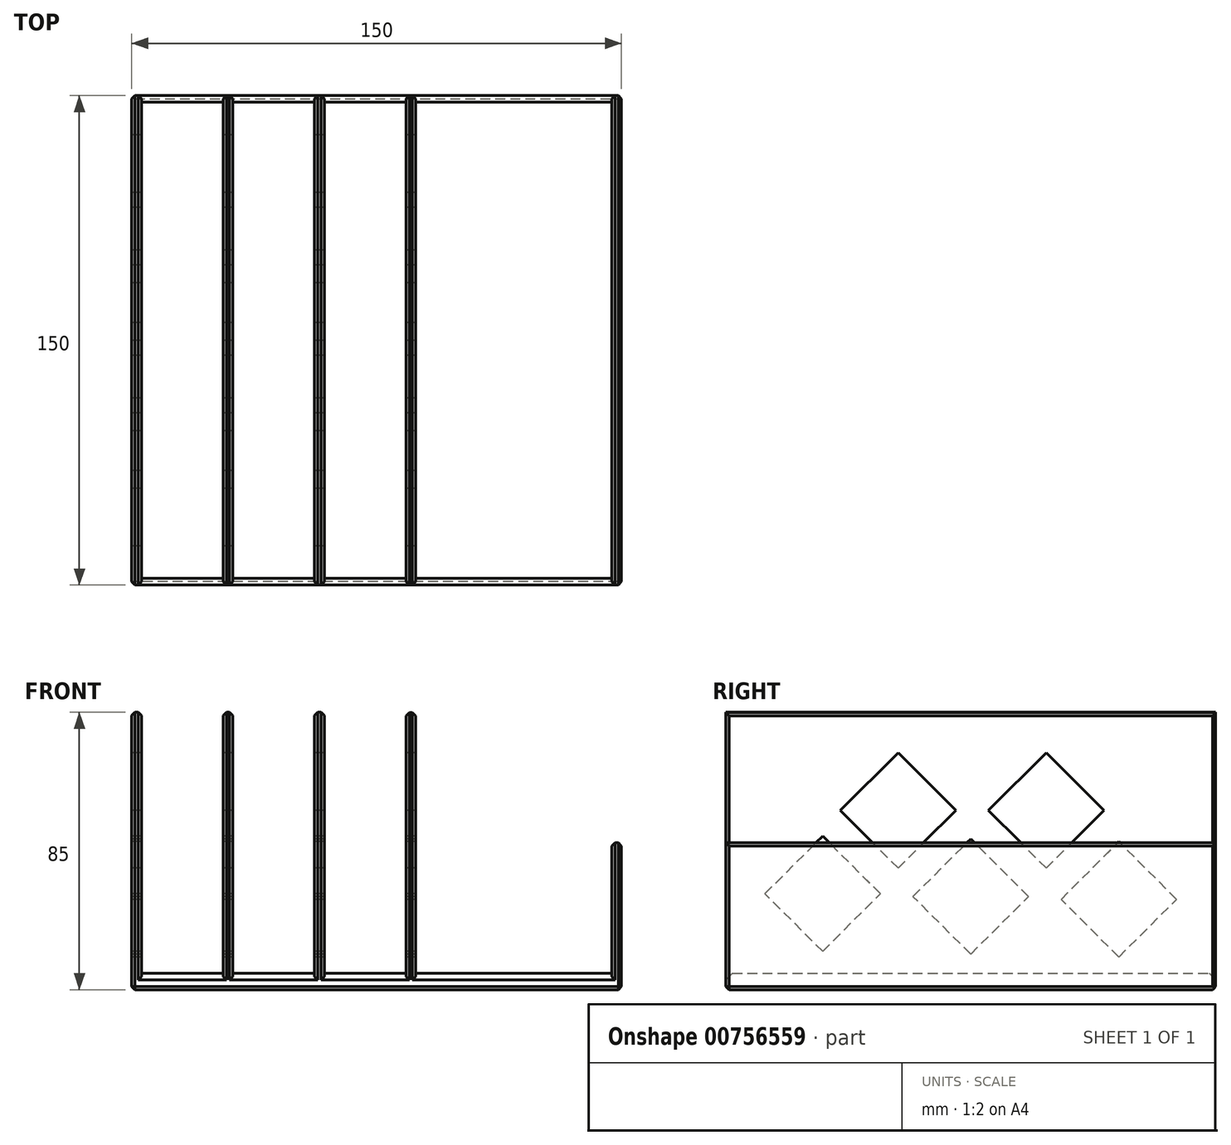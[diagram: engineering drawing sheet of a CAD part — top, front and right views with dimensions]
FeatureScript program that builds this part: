
annotation { "Feature Type Name" : "Feature", "Feature Type Description" : "" }
export const myFeature = defineFeature(function(context is Context, id is Id, definition is map)
    precondition{}
    {
        {
            var Q0;
            Q0=qCreatedBy(makeId("Front.planeOp"),FACE);
            var sketch = newSketch(context, id + "F0", { "sketchPlane" : qUnion([Q0])});
            skLineSegment(sketch, "E0.bottom", {"start": v(-63.24, 5) * mm, "end": v(86.76, 5) * mm});
            skLineSegment(sketch, "E0.top", {"start": v(-63.24, 0) * mm, "end": v(86.76, 0) * mm});
            skLineSegment(sketch, "E0.left", {"start": v(-63.24, 5) * mm, "end": v(-63.24, 0) * mm});
            skLineSegment(sketch, "E0.right", {"start": v(86.76, 5) * mm, "end": v(86.76, 0) * mm});
            skLineSegment(sketch, "E1.bottom", {"start": v(-63.24, 85) * mm, "end": v(-60.24, 85) * mm});
            skLineSegment(sketch, "E1.top", {"start": v(-63.24, 5) * mm, "end": v(-60.24, 5) * mm});
            skLineSegment(sketch, "E1.left", {"start": v(-63.24, 85) * mm, "end": v(-63.24, 5) * mm});
            skLineSegment(sketch, "E1.right", {"start": v(-60.24, 85) * mm, "end": v(-60.24, 5) * mm});
            skLineSegment(sketch, "E2.bottom", {"start": v(-35.24, 85) * mm, "end": v(-32.24, 85) * mm});
            skLineSegment(sketch, "E2.top", {"start": v(-35.24, 5) * mm, "end": v(-32.24, 5) * mm});
            skLineSegment(sketch, "E2.left", {"start": v(-35.24, 85) * mm, "end": v(-35.24, 5) * mm});
            skLineSegment(sketch, "E2.right", {"start": v(-32.24, 85) * mm, "end": v(-32.24, 5) * mm});
            skLineSegment(sketch, "E3.bottom", {"start": v(-7.24, 85) * mm, "end": v(-4.24, 85) * mm});
            skLineSegment(sketch, "E3.top", {"start": v(-7.24, 5) * mm, "end": v(-4.24, 5) * mm});
            skLineSegment(sketch, "E3.left", {"start": v(-7.24, 85) * mm, "end": v(-7.24, 5) * mm});
            skLineSegment(sketch, "E3.right", {"start": v(-4.24, 85) * mm, "end": v(-4.24, 5) * mm});
            skLineSegment(sketch, "E4.bottom", {"start": v(83.76, 45) * mm, "end": v(86.76, 45) * mm});
            skLineSegment(sketch, "E4.top", {"start": v(83.76, 5) * mm, "end": v(86.76, 5) * mm});
            skLineSegment(sketch, "E4.left", {"start": v(83.76, 45) * mm, "end": v(83.76, 5) * mm});
            skLineSegment(sketch, "E4.right", {"start": v(86.76, 45) * mm, "end": v(86.76, 5) * mm});
            skLineSegment(sketch, "E5.bottom", {"start": v(20.76, 84.9) * mm, "end": v(23.76, 84.9) * mm});
            skLineSegment(sketch, "E5.top", {"start": v(20.76, 5) * mm, "end": v(23.76, 5) * mm});
            skLineSegment(sketch, "E5.left", {"start": v(20.76, 84.9) * mm, "end": v(20.76, 5) * mm});
            skLineSegment(sketch, "E5.right", {"start": v(23.76, 84.9) * mm, "end": v(23.76, 5) * mm});
            skSolve(sketch);
        }
        {
            var Q0;
            Q0 = qSketchRegion(id + "F0", true);
            extrude(context, id + "F1", {"entities" : qUnion([Q0]), "depth" : 150 * mm, "offsetDistance" : 25 * mm});
        }
        {
            var Q0;
            Q0=makeQuery(id+"F1.opExtrude","SWEPT_FACE",FACE,{"disambiguationData":[OSD([sQuery(id+"F0.wireOp",EDGE,"E0.left"),sQuery(id+"F0.wireOp",EDGE,"E1.left")])]});
            var sketch = newSketch(context, id + "F2", { "sketchPlane" : qUnion([Q0])});
            skLineSegment(sketch, "E6.bottom", {"start": v(29.68, 45.36) * mm, "end": v(47.36, 27.68) * mm});
            skLineSegment(sketch, "E6.top", {"start": v(12, 27.68) * mm, "end": v(29.68, 10) * mm});
            skLineSegment(sketch, "E6.left", {"start": v(29.68, 45.36) * mm, "end": v(12, 27.68) * mm});
            skLineSegment(sketch, "E6.right", {"start": v(47.36, 27.68) * mm, "end": v(29.68, 10) * mm});
            skPoint(sketch, "E7", {"position": v(20.84, 36.52) * mm});
            skLineSegment(sketch, "E8.bottom", {"start": v(75.03, 46.21) * mm, "end": v(92.71, 28.54) * mm});
            skLineSegment(sketch, "E8.top", {"start": v(57.36, 28.54) * mm, "end": v(75.03, 10.86) * mm});
            skLineSegment(sketch, "E8.left", {"start": v(75.03, 46.21) * mm, "end": v(57.36, 28.54) * mm});
            skLineSegment(sketch, "E8.right", {"start": v(92.71, 28.54) * mm, "end": v(75.03, 10.86) * mm});
            skPoint(sketch, "E9", {"position": v(66.2, 37.38) * mm});
            skLineSegment(sketch, "E10.bottom", {"start": v(120.39, 47.07) * mm, "end": v(138.07, 29.4) * mm});
            skLineSegment(sketch, "E10.top", {"start": v(102.71, 29.4) * mm, "end": v(120.39, 11.72) * mm});
            skLineSegment(sketch, "E10.left", {"start": v(120.39, 47.07) * mm, "end": v(102.71, 29.4) * mm});
            skLineSegment(sketch, "E10.right", {"start": v(138.07, 29.4) * mm, "end": v(120.39, 11.72) * mm});
            skPoint(sketch, "E11", {"position": v(111.55, 38.23) * mm});
            skLineSegment(sketch, "E12.bottom", {"start": v(51.93, 72.6) * mm, "end": v(69.6, 54.93) * mm});
            skLineSegment(sketch, "E12.top", {"start": v(34.25, 54.93) * mm, "end": v(51.93, 37.25) * mm});
            skLineSegment(sketch, "E12.left", {"start": v(51.93, 72.6) * mm, "end": v(34.25, 54.93) * mm});
            skLineSegment(sketch, "E12.right", {"start": v(69.6, 54.93) * mm, "end": v(51.93, 37.25) * mm});
            skPoint(sketch, "E13", {"position": v(43.09, 63.77) * mm});
            skLineSegment(sketch, "E14.bottom", {"start": v(97.28, 72.6) * mm, "end": v(114.96, 54.93) * mm});
            skLineSegment(sketch, "E14.top", {"start": v(79.6, 54.93) * mm, "end": v(97.28, 37.25) * mm});
            skLineSegment(sketch, "E14.left", {"start": v(97.28, 72.6) * mm, "end": v(79.6, 54.93) * mm});
            skLineSegment(sketch, "E14.right", {"start": v(114.96, 54.93) * mm, "end": v(97.28, 37.25) * mm});
            skPoint(sketch, "E15", {"position": v(88.44, 63.77) * mm});
            skSolve(sketch);
        }
        {
            var Q0;
            Q0 = qSketchRegion(id + "F2", true);
            extrude(context, id + "F3", {"entities" : qUnion([Q0]), "operationType" : NewBodyOperationType.REMOVE, "oppositeDirection" : true, "depth" : 120 * mm, "offsetDistance" : 25 * mm});
        }
        {
            var Q0;
            {var subQ0=sQuery(id+"F0.wireOp",EDGE,"E0.bottom");Q0=makeQuery(id+"F1.opExtrude","CAP_EDGE",EDGE,{"disambiguationData":[OSD([subQ0]),TDD([makeQuery(id+"F0.imprint","IMPRINT",EDGE,{"disambiguationData":[TD([[makeQuery(id+"F0.imprint","INTERSECT",VERTEX,{"derivedFrom":[subQ0,sQuery(id+"F0.wireOp",EDGE,"E4.top"),sQuery(id+"F0.wireOp",EDGE,"E4.left")]}),1.0]])],"derivedFrom":subQ0})])],"isStart":false});}
            var Q1;
            {var subQ0=sQuery(id+"F0.wireOp",EDGE,"E0.bottom");Q1=makeQuery(id+"F1.opExtrude","CAP_EDGE",EDGE,{"disambiguationData":[OSD([subQ0]),TDD([makeQuery(id+"F0.imprint","IMPRINT",EDGE,{"disambiguationData":[TD([[makeQuery(id+"F0.imprint","INTERSECT",VERTEX,{"derivedFrom":[subQ0,sQuery(id+"F0.wireOp",EDGE,"E3.top"),sQuery(id+"F0.wireOp",EDGE,"E3.right")]}),-1.0]])],"derivedFrom":subQ0})])],"isStart":false});}
            var Q2;
            {var subQ0=sQuery(id+"F0.wireOp",EDGE,"E0.bottom");Q2=makeQuery(id+"F1.opExtrude","CAP_EDGE",EDGE,{"disambiguationData":[OSD([subQ0]),TDD([makeQuery(id+"F0.imprint","IMPRINT",EDGE,{"disambiguationData":[TD([[makeQuery(id+"F0.imprint","INTERSECT",VERTEX,{"derivedFrom":[subQ0,sQuery(id+"F0.wireOp",EDGE,"E2.top"),sQuery(id+"F0.wireOp",EDGE,"E2.right")]}),-1.0]])],"derivedFrom":subQ0})])],"isStart":false});}
            var Q3;
            {var subQ0=sQuery(id+"F0.wireOp",EDGE,"E0.bottom");Q3=makeQuery(id+"F1.opExtrude","CAP_EDGE",EDGE,{"disambiguationData":[OSD([subQ0]),TDD([makeQuery(id+"F0.imprint","IMPRINT",EDGE,{"disambiguationData":[TD([[makeQuery(id+"F0.imprint","INTERSECT",VERTEX,{"derivedFrom":[subQ0,sQuery(id+"F0.wireOp",EDGE,"E1.top"),sQuery(id+"F0.wireOp",EDGE,"E1.right")]}),-1.0]])],"derivedFrom":subQ0})])],"isStart":false});}
            var Q4;
            {var subQ0=sQuery(id+"F0.wireOp",EDGE,"E0.bottom");Q4=makeQuery(id+"F1.opExtrude","CAP_EDGE",EDGE,{"disambiguationData":[OSD([subQ0]),TDD([makeQuery(id+"F0.imprint","IMPRINT",EDGE,{"disambiguationData":[TD([[makeQuery(id+"F0.imprint","INTERSECT",VERTEX,{"derivedFrom":[subQ0,sQuery(id+"F0.wireOp",EDGE,"E1.top"),sQuery(id+"F0.wireOp",EDGE,"E1.right")]}),-1.0]])],"derivedFrom":subQ0})])],"isStart":true});}
            var Q5;
            {var subQ0=sQuery(id+"F0.wireOp",EDGE,"E0.bottom");Q5=makeQuery(id+"F1.opExtrude","CAP_EDGE",EDGE,{"disambiguationData":[OSD([subQ0]),TDD([makeQuery(id+"F0.imprint","IMPRINT",EDGE,{"disambiguationData":[TD([[makeQuery(id+"F0.imprint","INTERSECT",VERTEX,{"derivedFrom":[subQ0,sQuery(id+"F0.wireOp",EDGE,"E2.top"),sQuery(id+"F0.wireOp",EDGE,"E2.right")]}),-1.0]])],"derivedFrom":subQ0})])],"isStart":true});}
            var Q6;
            {var subQ0=sQuery(id+"F0.wireOp",EDGE,"E0.bottom");Q6=makeQuery(id+"F1.opExtrude","CAP_EDGE",EDGE,{"disambiguationData":[OSD([subQ0]),TDD([makeQuery(id+"F0.imprint","IMPRINT",EDGE,{"disambiguationData":[TD([[makeQuery(id+"F0.imprint","INTERSECT",VERTEX,{"derivedFrom":[subQ0,sQuery(id+"F0.wireOp",EDGE,"E3.top"),sQuery(id+"F0.wireOp",EDGE,"E3.right")]}),-1.0]])],"derivedFrom":subQ0})])],"isStart":true});}
            var Q7;
            {var subQ0=sQuery(id+"F0.wireOp",EDGE,"E0.bottom");Q7=makeQuery(id+"F1.opExtrude","CAP_EDGE",EDGE,{"disambiguationData":[OSD([subQ0]),TDD([makeQuery(id+"F0.imprint","IMPRINT",EDGE,{"disambiguationData":[TD([[makeQuery(id+"F0.imprint","INTERSECT",VERTEX,{"derivedFrom":[subQ0,sQuery(id+"F0.wireOp",EDGE,"E4.top"),sQuery(id+"F0.wireOp",EDGE,"E4.left")]}),1.0]])],"derivedFrom":subQ0})])],"isStart":true});}
            chamfer(context, id + "F4", {"entities" : qUnion([Q0, Q1, Q2, Q3, Q4, Q5, Q6, Q7]), "width" : 2 * mm, "tangentPropagation" : true});
        }
        {
            var Q0;
            Q0=makeQuery(id+"F1.opExtrude","SWEPT_EDGE",EDGE,{"disambiguationData":[OSD([sQuery(id+"F0.wireOp",EDGE,"E0.top"),sQuery(id+"F0.wireOp",EDGE,"E0.left")])]});
            var Q1;
            Q1=makeQuery(id+"F1.opExtrude","CAP_EDGE",EDGE,{"disambiguationData":[OSD([sQuery(id+"F0.wireOp",EDGE,"E0.top")])],"isStart":false});
            var Q2;
            Q2=makeQuery(id+"F1.opExtrude","SWEPT_EDGE",EDGE,{"disambiguationData":[OSD([sQuery(id+"F0.wireOp",EDGE,"E0.top"),sQuery(id+"F0.wireOp",EDGE,"E0.right")])]});
            var Q3;
            Q3=makeQuery(id+"F1.opExtrude","CAP_EDGE",EDGE,{"disambiguationData":[OSD([sQuery(id+"F0.wireOp",EDGE,"E0.top")])],"isStart":true});
            var Q4;
            Q4=makeQuery(id+"F1.opExtrude","CAP_EDGE",EDGE,{"disambiguationData":[OSD([sQuery(id+"F0.wireOp",EDGE,"E4.left")])],"isStart":false});
            var Q5;
            Q5=makeQuery(id+"F1.opExtrude","CAP_EDGE",EDGE,{"disambiguationData":[OSD([sQuery(id+"F0.wireOp",EDGE,"E5.left")])],"isStart":false});
            var Q6;
            Q6=makeQuery(id+"F1.opExtrude","CAP_EDGE",EDGE,{"disambiguationData":[OSD([sQuery(id+"F0.wireOp",EDGE,"E3.left")])],"isStart":false});
            var Q7;
            Q7=makeQuery(id+"F1.opExtrude","CAP_EDGE",EDGE,{"disambiguationData":[OSD([sQuery(id+"F0.wireOp",EDGE,"E2.left")])],"isStart":false});
            var Q8;
            Q8=makeQuery(id+"F1.opExtrude","CAP_EDGE",EDGE,{"disambiguationData":[OSD([sQuery(id+"F0.wireOp",EDGE,"E0.left"),sQuery(id+"F0.wireOp",EDGE,"E1.left")])],"isStart":false});
            var Q9;
            Q9=makeQuery(id+"F1.opExtrude","CAP_EDGE",EDGE,{"disambiguationData":[OSD([sQuery(id+"F0.wireOp",EDGE,"E0.right"),sQuery(id+"F0.wireOp",EDGE,"E4.right")])],"isStart":false});
            var Q10;
            Q10=makeQuery(id+"F1.opExtrude","CAP_EDGE",EDGE,{"disambiguationData":[OSD([sQuery(id+"F0.wireOp",EDGE,"E5.right")])],"isStart":false});
            var Q11;
            Q11=makeQuery(id+"F1.opExtrude","CAP_EDGE",EDGE,{"disambiguationData":[OSD([sQuery(id+"F0.wireOp",EDGE,"E3.right")])],"isStart":false});
            var Q12;
            Q12=makeQuery(id+"F1.opExtrude","CAP_EDGE",EDGE,{"disambiguationData":[OSD([sQuery(id+"F0.wireOp",EDGE,"E2.right")])],"isStart":false});
            var Q13;
            Q13=makeQuery(id+"F1.opExtrude","CAP_EDGE",EDGE,{"disambiguationData":[OSD([sQuery(id+"F0.wireOp",EDGE,"E1.right")])],"isStart":false});
            chamfer(context, id + "F5", {"entities" : qUnion([Q0, Q1, Q2, Q3, Q4, Q5, Q6, Q7, Q8, Q9, Q10, Q11, Q12, Q13]), "width" : 1 * mm, "tangentPropagation" : true});
        }
        {
            var Q0;
            Q0=makeQuery(id+"F1.opExtrude","CAP_EDGE",EDGE,{"disambiguationData":[OSD([sQuery(id+"F0.wireOp",EDGE,"E4.left")])],"isStart":true});
            var Q1;
            Q1=makeQuery(id+"F1.opExtrude","CAP_EDGE",EDGE,{"disambiguationData":[OSD([sQuery(id+"F0.wireOp",EDGE,"E0.right"),sQuery(id+"F0.wireOp",EDGE,"E4.right")])],"isStart":true});
            var Q2;
            Q2=makeQuery(id+"F1.opExtrude","CAP_EDGE",EDGE,{"disambiguationData":[OSD([sQuery(id+"F0.wireOp",EDGE,"E5.right")])],"isStart":true});
            var Q3;
            Q3=makeQuery(id+"F1.opExtrude","CAP_EDGE",EDGE,{"disambiguationData":[OSD([sQuery(id+"F0.wireOp",EDGE,"E5.left")])],"isStart":true});
            var Q4;
            Q4=makeQuery(id+"F1.opExtrude","CAP_EDGE",EDGE,{"disambiguationData":[OSD([sQuery(id+"F0.wireOp",EDGE,"E3.right")])],"isStart":true});
            var Q5;
            Q5=makeQuery(id+"F1.opExtrude","CAP_EDGE",EDGE,{"disambiguationData":[OSD([sQuery(id+"F0.wireOp",EDGE,"E3.left")])],"isStart":true});
            var Q6;
            Q6=makeQuery(id+"F1.opExtrude","CAP_EDGE",EDGE,{"disambiguationData":[OSD([sQuery(id+"F0.wireOp",EDGE,"E2.right")])],"isStart":true});
            var Q7;
            Q7=makeQuery(id+"F1.opExtrude","CAP_EDGE",EDGE,{"disambiguationData":[OSD([sQuery(id+"F0.wireOp",EDGE,"E2.left")])],"isStart":true});
            var Q8;
            Q8=makeQuery(id+"F1.opExtrude","CAP_EDGE",EDGE,{"disambiguationData":[OSD([sQuery(id+"F0.wireOp",EDGE,"E1.right")])],"isStart":true});
            var Q9;
            Q9=makeQuery(id+"F1.opExtrude","CAP_EDGE",EDGE,{"disambiguationData":[OSD([sQuery(id+"F0.wireOp",EDGE,"E0.left"),sQuery(id+"F0.wireOp",EDGE,"E1.left")])],"isStart":true});
            chamfer(context, id + "F6", {"entities" : qUnion([Q0, Q1, Q2, Q3, Q4, Q5, Q6, Q7, Q8, Q9]), "width" : 1 * mm, "tangentPropagation" : true});
        }
        {
            var Q0;
            Q0=makeQuery(id+"F1.opExtrude","SWEPT_EDGE",EDGE,{"disambiguationData":[OSD([sQuery(id+"F0.wireOp",EDGE,"E4.bottom"),sQuery(id+"F0.wireOp",EDGE,"E4.right")])]});
            var Q1;
            Q1=makeQuery(id+"F1.opExtrude","SWEPT_EDGE",EDGE,{"disambiguationData":[OSD([sQuery(id+"F0.wireOp",EDGE,"E4.bottom"),sQuery(id+"F0.wireOp",EDGE,"E4.left")])]});
            var Q2;
            Q2=makeQuery(id+"F1.opExtrude","SWEPT_EDGE",EDGE,{"disambiguationData":[OSD([sQuery(id+"F0.wireOp",EDGE,"E5.bottom"),sQuery(id+"F0.wireOp",EDGE,"E5.right")])]});
            var Q3;
            Q3=makeQuery(id+"F1.opExtrude","SWEPT_EDGE",EDGE,{"disambiguationData":[OSD([sQuery(id+"F0.wireOp",EDGE,"E5.bottom"),sQuery(id+"F0.wireOp",EDGE,"E5.left")])]});
            var Q4;
            Q4=makeQuery(id+"F1.opExtrude","SWEPT_EDGE",EDGE,{"disambiguationData":[OSD([sQuery(id+"F0.wireOp",EDGE,"E3.bottom"),sQuery(id+"F0.wireOp",EDGE,"E3.right")])]});
            var Q5;
            Q5=makeQuery(id+"F1.opExtrude","SWEPT_EDGE",EDGE,{"disambiguationData":[OSD([sQuery(id+"F0.wireOp",EDGE,"E3.bottom"),sQuery(id+"F0.wireOp",EDGE,"E3.left")])]});
            var Q6;
            Q6=makeQuery(id+"F1.opExtrude","SWEPT_EDGE",EDGE,{"disambiguationData":[OSD([sQuery(id+"F0.wireOp",EDGE,"E2.bottom"),sQuery(id+"F0.wireOp",EDGE,"E2.right")])]});
            var Q7;
            Q7=makeQuery(id+"F1.opExtrude","SWEPT_EDGE",EDGE,{"disambiguationData":[OSD([sQuery(id+"F0.wireOp",EDGE,"E2.bottom"),sQuery(id+"F0.wireOp",EDGE,"E2.left")])]});
            var Q8;
            Q8=makeQuery(id+"F1.opExtrude","SWEPT_EDGE",EDGE,{"disambiguationData":[OSD([sQuery(id+"F0.wireOp",EDGE,"E1.bottom"),sQuery(id+"F0.wireOp",EDGE,"E1.right")])]});
            var Q9;
            Q9=makeQuery(id+"F1.opExtrude","SWEPT_EDGE",EDGE,{"disambiguationData":[OSD([sQuery(id+"F0.wireOp",EDGE,"E1.bottom"),sQuery(id+"F0.wireOp",EDGE,"E1.left")])]});
            chamfer(context, id + "F7", {"entities" : qUnion([Q0, Q1, Q2, Q3, Q4, Q5, Q6, Q7, Q8, Q9]), "width" : 1 * mm, "tangentPropagation" : true});
        }
        {
            var Q0;
            Q0=makeQuery(id+"F1.opExtrude","SWEPT_BODY",BODY,{"disambiguationData":[OSD([sQuery(id+"F0.wireOp",EDGE,"E0.bottom"),sQuery(id+"F0.wireOp",EDGE,"E0.top"),sQuery(id+"F0.wireOp",EDGE,"E0.left"),sQuery(id+"F0.wireOp",EDGE,"E0.right"),sQuery(id+"F0.wireOp",EDGE,"E1.bottom"),sQuery(id+"F0.wireOp",EDGE,"E1.left"),sQuery(id+"F0.wireOp",EDGE,"E1.right"),sQuery(id+"F0.wireOp",EDGE,"E2.bottom"),sQuery(id+"F0.wireOp",EDGE,"E2.left"),sQuery(id+"F0.wireOp",EDGE,"E2.right"),sQuery(id+"F0.wireOp",EDGE,"E3.bottom"),sQuery(id+"F0.wireOp",EDGE,"E3.left"),sQuery(id+"F0.wireOp",EDGE,"E3.right"),sQuery(id+"F0.wireOp",EDGE,"E4.bottom"),sQuery(id+"F0.wireOp",EDGE,"E4.left"),sQuery(id+"F0.wireOp",EDGE,"E4.right"),sQuery(id+"F0.wireOp",EDGE,"E5.bottom"),sQuery(id+"F0.wireOp",EDGE,"E5.left"),sQuery(id+"F0.wireOp",EDGE,"E5.right")])]});
            transform(context, id + "F8", {"entities" : qUnion([Q0]), "transformType" : TransformType.TRANSLATION_3D, "dx" : -12 * mm, "dy" : 75 * mm, "dz" : 0 * mm, "makeCopy" : false});
        }
    });
